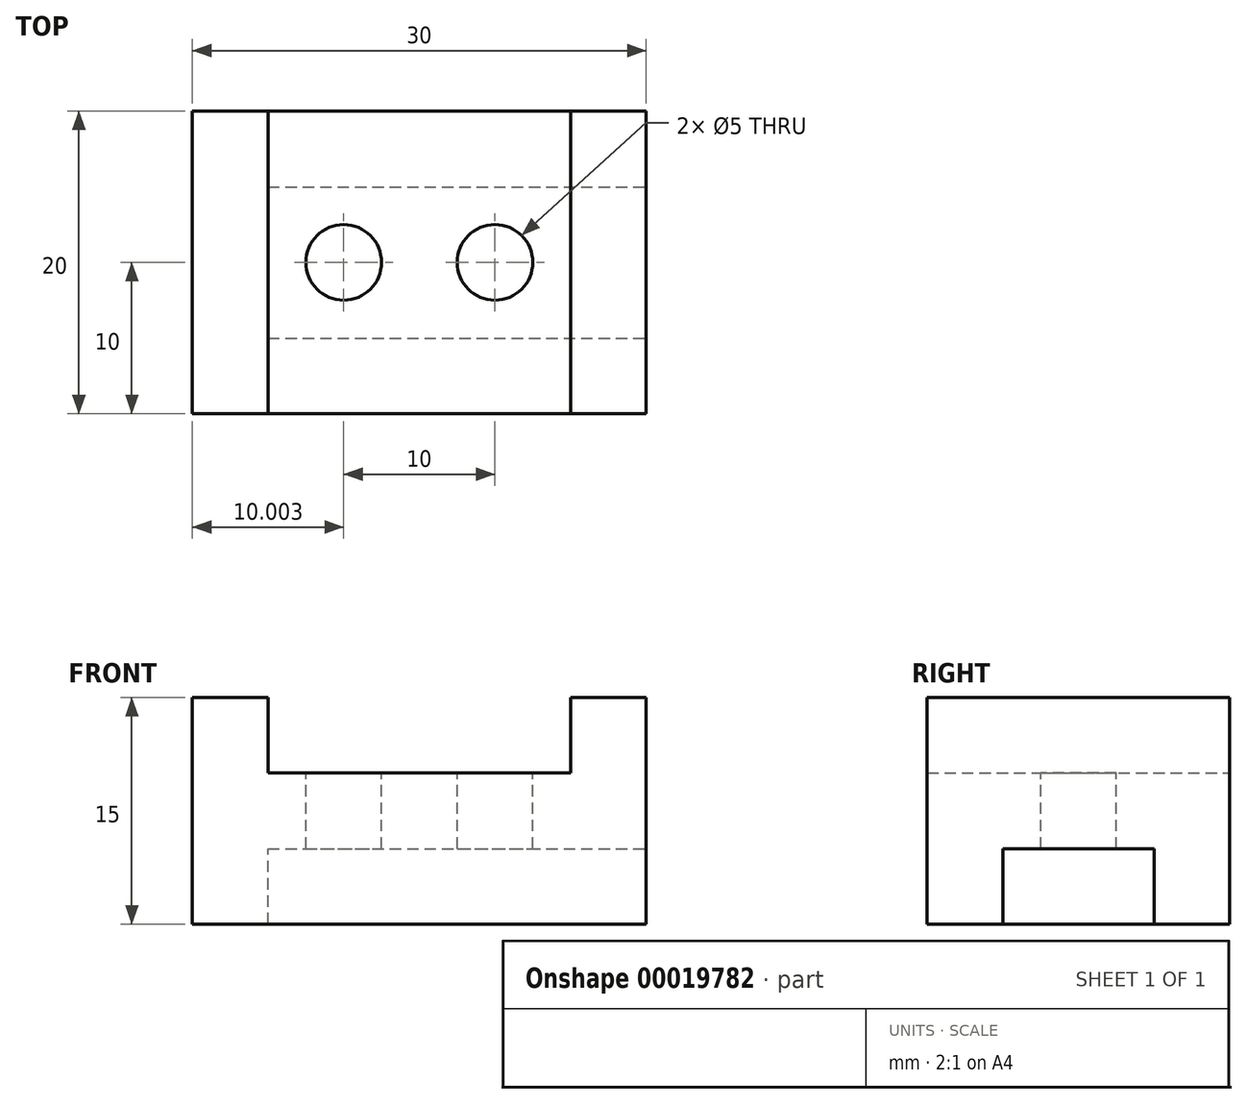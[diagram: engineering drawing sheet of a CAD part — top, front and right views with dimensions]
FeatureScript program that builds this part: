
annotation { "Feature Type Name" : "Feature", "Feature Type Description" : "" }
export const myFeature = defineFeature(function(context is Context, id is Id, definition is map)
    precondition{}
    {
        {
            var Q0;
            Q0=qCreatedBy(makeId("Front.planeOp"),FACE);
            var sketch = newSketch(context, id + "F0", { "sketchPlane" : qUnion([Q0])});
            skLineSegment(sketch, "E0", {"start": v(-24.45, -17.4) * mm, "end": v(5.55, -17.4) * mm});
            skLineSegment(sketch, "E1", {"start": v(5.55, -17.4) * mm, "end": v(5.55, -2.4) * mm});
            skLineSegment(sketch, "E2", {"start": v(5.55, -2.4) * mm, "end": v(0.55, -2.4) * mm});
            skLineSegment(sketch, "E3", {"start": v(0.55, -2.4) * mm, "end": v(0.55, -7.4) * mm});
            skLineSegment(sketch, "E4", {"start": v(0.55, -7.4) * mm, "end": v(-19.45, -7.4) * mm});
            skLineSegment(sketch, "E5", {"start": v(-19.45, -7.4) * mm, "end": v(-19.45, -2.4) * mm});
            skLineSegment(sketch, "E6", {"start": v(-19.45, -2.4) * mm, "end": v(-24.45, -2.4) * mm});
            skLineSegment(sketch, "E7", {"start": v(-24.45, -2.4) * mm, "end": v(-24.45, -17.4) * mm});
            skSolve(sketch);
        }
        {
            var Q0;
            Q0=makeQuery(id+"F0.imprint","IMPRINT",FACE,{"disambiguationData":[TD([[makeQuery(id+"F0.imprint","IMPRINT",EDGE,{"derivedFrom":sQuery(id+"F0.wireOp",EDGE,"E0")}),1.0]])]});
            extrude(context, id + "F1", {"entities" : qUnion([Q0]), "depth" : 20 * mm});
        }
        {
            var Q0;
            Q0=makeQuery(id+"F1.opExtrude","SWEPT_FACE",FACE,{"disambiguationData":[OSD([sQuery(id+"F0.wireOp",EDGE,"E1")])]});
            var sketch = newSketch(context, id + "F2", { "sketchPlane" : qUnion([Q0])});
            skLineSegment(sketch, "E8", {"start": v(-15, -17.4) * mm, "end": v(-15, -12.4) * mm});
            skLineSegment(sketch, "E9", {"start": v(-15, -12.4) * mm, "end": v(-5, -12.4) * mm});
            skLineSegment(sketch, "E10", {"start": v(-5, -12.4) * mm, "end": v(-5, -17.4) * mm});
            skLineSegment(sketch, "E11", {"start": v(-5, -17.4) * mm, "end": v(-15, -17.4) * mm});
            skLineSegment(sketch, "E12", {"start": v(-20, -17.4) * mm, "end": v(-15, -17.4) * mm});
            skLineSegment(sketch, "E13", {"start": v(-15, -17.4) * mm, "end": v(-5, -17.4) * mm});
            skLineSegment(sketch, "E14", {"start": v(-5, -17.4) * mm, "end": v(0, -17.4) * mm});
            skLineSegment(sketch, "E15", {"start": v(0, -17.4) * mm, "end": v(-5, -17.4) * mm});
            skSolve(sketch);
        }
        {
            var Q0;
            Q0=makeQuery(id+"F2.imprint","IMPRINT",FACE,{"disambiguationData":[TD([[makeQuery(id+"F2.imprint","IMPRINT",EDGE,{"derivedFrom":sQuery(id+"F2.wireOp",EDGE,"E8")}),-1.0]])]});
            extrude(context, id + "F3", {"entities" : qUnion([Q0]), "operationType" : NewBodyOperationType.REMOVE, "oppositeDirection" : true, "depth" : 25 * mm});
        }
        {
            var Q0;
            Q0=makeQuery(id+"F1.opExtrude","SWEPT_FACE",FACE,{"disambiguationData":[OSD([sQuery(id+"F0.wireOp",EDGE,"E4")])]});
            var sketch = newSketch(context, id + "F4", { "sketchPlane" : qUnion([Q0])});
            skLineSegment(sketch, "E16", {"start": v(-19.45, -20) * mm, "end": v(-14.45, -20) * mm});
            skLineSegment(sketch, "E17", {"start": v(-14.45, -20) * mm, "end": v(-4.45, -20) * mm});
            skLineSegment(sketch, "E18", {"start": v(-4.45, -20) * mm, "end": v(0.55, -20) * mm});
            skCircle(sketch, "E19", {"center": v(-14.45, -10) * mm, "radius": 2.5 * mm});
            skCircle(sketch, "E20", {"center": v(-4.45, -10) * mm, "radius": 2.5 * mm});
            skSolve(sketch);
        }
        {
            var Q0;
            Q0=makeQuery(id+"F4.imprint","IMPRINT",FACE,{"disambiguationData":[TD([[makeQuery(id+"F4.imprint","IMPRINT",EDGE,{"derivedFrom":sQuery(id+"F4.wireOp",EDGE,"E19")}),1.0]])]});
            var Q1;
            Q1=makeQuery(id+"F4.imprint","IMPRINT",FACE,{"disambiguationData":[TD([[makeQuery(id+"F4.imprint","IMPRINT",EDGE,{"derivedFrom":sQuery(id+"F4.wireOp",EDGE,"E20")}),1.0]])]});
            extrude(context, id + "F5", {"entities" : qUnion([Q0, Q1]), "operationType" : NewBodyOperationType.REMOVE, "oppositeDirection" : true, "depth" : 25 * mm});
        }
    });
